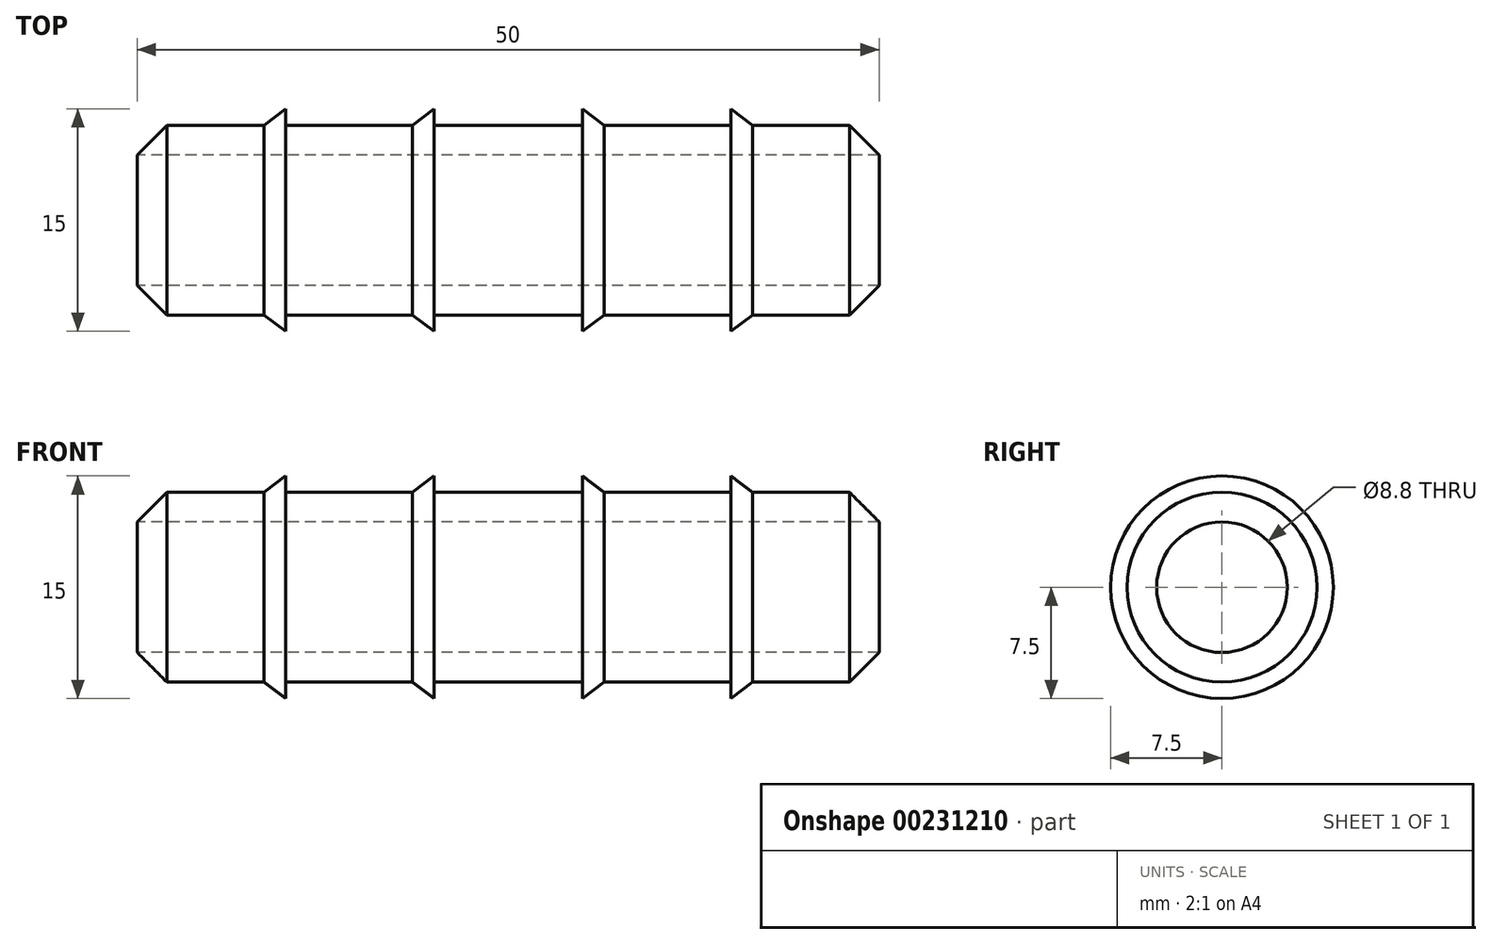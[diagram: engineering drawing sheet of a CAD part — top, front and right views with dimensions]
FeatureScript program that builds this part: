
annotation { "Feature Type Name" : "Feature", "Feature Type Description" : "" }
export const myFeature = defineFeature(function(context is Context, id is Id, definition is map)
    precondition{}
    {
        {
            var Q0;
            Q0=qCreatedBy(makeId("Right.planeOp"),FACE);
            var sketch = newSketch(context, id + "F0", { "sketchPlane" : qUnion([Q0])});
            skCircle(sketch, "E0", {"center": v(0, 0) * mm, "radius": 6.4 * mm});
            skSolve(sketch);
        }
        {
            var Q0;
            Q0 = qSketchRegion(id + "F0", true);
            extrude(context, id + "F1", {"entities" : qUnion([Q0]), "depth" : 50 * mm});
        }
        {
            var Q0;
            Q0=qCreatedBy(makeId("Front.planeOp"),FACE);
            var sketch = newSketch(context, id + "F2", { "sketchPlane" : qUnion([Q0])});
            skLineSegment(sketch, "E1.bottom", {"start": v(0, 7.5) * mm, "end": v(50, 7.5) * mm});
            skLineSegment(sketch, "E1.top", {"start": v(0, -7.5) * mm, "end": v(50, -7.5) * mm});
            skLineSegment(sketch, "E1.left", {"start": v(0, 7.5) * mm, "end": v(0, -7.5) * mm});
            skLineSegment(sketch, "E1.right", {"start": v(50, 7.5) * mm, "end": v(50, -7.5) * mm});
            skLineSegment(sketch, "E2", {"start": v(0, 0) * mm, "end": v(50, 0) * mm});
            skLineSegment(sketch, "E3", {"start": v(0, 0) * mm, "end": v(10, 7.5) * mm});
            skLineSegment(sketch, "E4", {"start": v(10, 7.5) * mm, "end": v(10, -7.5) * mm});
            skLineSegment(sketch, "E5", {"start": v(10, -7.5) * mm, "end": v(0, 0) * mm});
            skLineSegment(sketch, "E6", {"start": v(10, 0) * mm, "end": v(20, 7.5) * mm});
            skLineSegment(sketch, "E7", {"start": v(20, 7.5) * mm, "end": v(20, -7.5) * mm});
            skLineSegment(sketch, "E8", {"start": v(20, -7.5) * mm, "end": v(10, 0) * mm});
            skLineSegment(sketch, "E9", {"start": v(50, 0) * mm, "end": v(40, 7.5) * mm});
            skLineSegment(sketch, "E10", {"start": v(40, 7.5) * mm, "end": v(40, -7.5) * mm});
            skLineSegment(sketch, "E11", {"start": v(40, -7.5) * mm, "end": v(50, 0) * mm});
            skLineSegment(sketch, "E12", {"start": v(40, 0) * mm, "end": v(30, 7.5) * mm});
            skLineSegment(sketch, "E13", {"start": v(30, 7.5) * mm, "end": v(30, -7.5) * mm});
            skLineSegment(sketch, "E14", {"start": v(30, -7.5) * mm, "end": v(40, 0) * mm});
            skSolve(sketch);
        }
        {
            var Q0;
            {var subQ0=sQuery(id+"F2.wireOp",EDGE,"E3");Q0=makeQuery(id+"F2.imprint","IMPRINT",FACE,{"disambiguationData":[TD([[makeQuery(id+"F2.imprint","IMPRINT",EDGE,{"derivedFrom":subQ0}),-1.0]])]});}
            var Q1;
            {var subQ0=sQuery(id+"F2.wireOp",EDGE,"E6");Q1=makeQuery(id+"F2.imprint","IMPRINT",FACE,{"disambiguationData":[TD([[makeQuery(id+"F2.imprint","IMPRINT",EDGE,{"derivedFrom":subQ0}),-1.0]])]});}
            var Q2;
            {var subQ0=sQuery(id+"F2.wireOp",EDGE,"E12");Q2=makeQuery(id+"F2.imprint","IMPRINT",FACE,{"disambiguationData":[TD([[makeQuery(id+"F2.imprint","IMPRINT",EDGE,{"derivedFrom":subQ0}),1.0]])]});}
            var Q3;
            {var subQ0=sQuery(id+"F2.wireOp",EDGE,"E9");Q3=makeQuery(id+"F2.imprint","IMPRINT",FACE,{"disambiguationData":[TD([[makeQuery(id+"F2.imprint","IMPRINT",EDGE,{"derivedFrom":subQ0}),1.0]])]});}
            var Q4;
            Q4=sQuery(id+"F2.wireOp",EDGE,"E2");
            revolve(context, id + "F3", {"operationType" : NewBodyOperationType.ADD, "entities" : qUnion([Q0, Q1, Q2, Q3]), "axis" : qUnion([Q4]), "revolveType" : RevolveType.FULL});
        }
        {
            var Q0;
            Q0=makeQuery(id+"F1.opExtrude","CAP_FACE",FACE,{"disambiguationData":[OSD([sQuery(id+"F0.wireOp",EDGE,"E0")])],"isStart":true});
            var sketch = newSketch(context, id + "F4", { "sketchPlane" : qUnion([Q0])});
            skCircle(sketch, "E15", {"center": v(0, 0) * mm, "radius": 4.4 * mm});
            skSolve(sketch);
        }
        {
            var Q0;
            Q0 = qSketchRegion(id + "F4", true);
            extrude(context, id + "F5", {"entities" : qUnion([Q0]), "operationType" : NewBodyOperationType.REMOVE, "endBound" : BoundingType.THROUGH_ALL, "oppositeDirection" : true, "depth" : 25 * mm});
        }
        {
            var Q0;
            Q0=makeQuery(id+"F1.opExtrude","CAP_EDGE",EDGE,{"disambiguationData":[OSD([sQuery(id+"F0.wireOp",EDGE,"E0")])],"isStart":false});
            var Q1;
            Q1=makeQuery(id+"F1.opExtrude","CAP_EDGE",EDGE,{"disambiguationData":[OSD([sQuery(id+"F0.wireOp",EDGE,"E0")])],"isStart":true});
            chamfer(context, id + "F6", {"entities" : qUnion([Q0, Q1]), "width" : 2 * mm, "tangentPropagation" : true});
        }
    });
